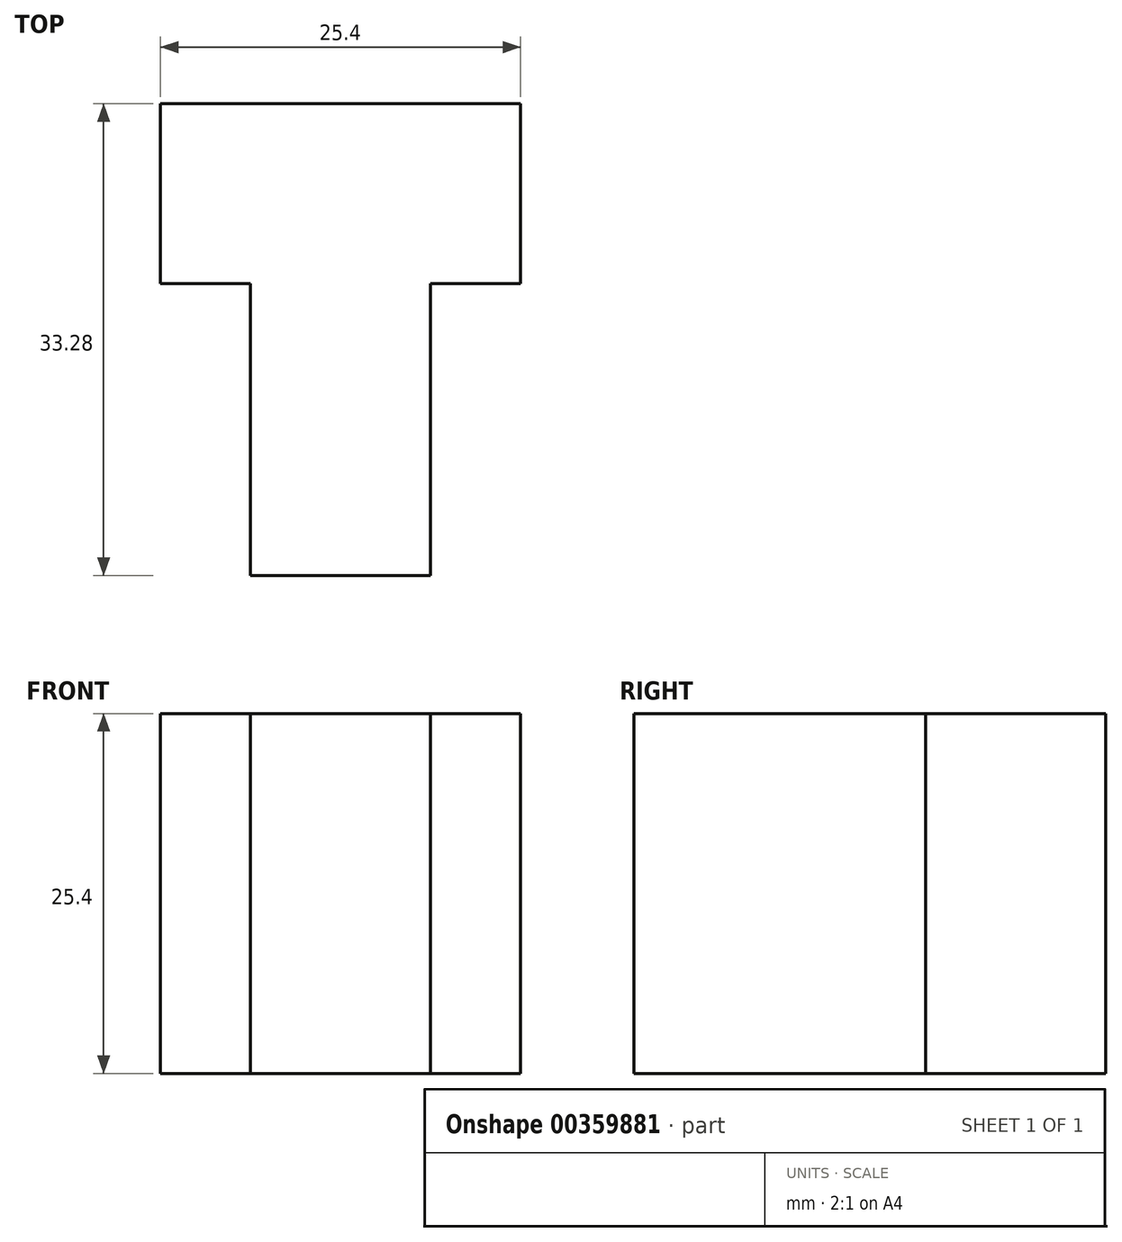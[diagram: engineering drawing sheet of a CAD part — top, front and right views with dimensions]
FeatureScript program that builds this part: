
annotation { "Feature Type Name" : "Feature", "Feature Type Description" : "" }
export const myFeature = defineFeature(function(context is Context, id is Id, definition is map)
    precondition{}
    {
        {
            var Q0;
            Q0=qCreatedBy(makeId("Top.planeOp"),FACE);
            var sketch = newSketch(context, id + "F0", { "sketchPlane" : qUnion([Q0])});
            skLineSegment(sketch, "E0", {"start": v(0, 12.7) * mm, "end": v(0, 0) * mm});
            skLineSegment(sketch, "E1", {"start": v(0, 0) * mm, "end": v(6.35, 0) * mm});
            skLineSegment(sketch, "E2", {"start": v(0, 12.7) * mm, "end": v(25.4, 12.7) * mm});
            skLineSegment(sketch, "E3", {"start": v(25.4, 0) * mm, "end": v(25.4, 12.7) * mm});
            skLineSegment(sketch, "E4", {"start": v(6.35, 0) * mm, "end": v(6.35, -20.58) * mm});
            skLineSegment(sketch, "E5", {"start": v(25.4, 0) * mm, "end": v(19.05, 0) * mm});
            skLineSegment(sketch, "E6", {"start": v(19.05, 0) * mm, "end": v(19.05, -20.58) * mm});
            skLineSegment(sketch, "E7", {"start": v(6.35, -20.58) * mm, "end": v(19.05, -20.58) * mm});
            skSolve(sketch);
        }
        {
            var Q0;
            Q0 = qSketchRegion(id + "F0", true);
            extrude(context, id + "F1", {"entities" : qUnion([Q0]), "depth" : 25.4 * mm});
        }
    });
